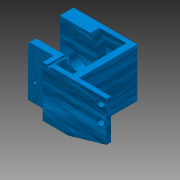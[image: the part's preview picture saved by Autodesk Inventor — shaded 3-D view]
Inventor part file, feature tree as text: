
AUTODESK INVENTOR PART (.ipt)
format: ipt  version: 2015 (Build 190159000, 159)  size: 166,400 bytes
history: native  units: in
note: dims shown in document units (in); Inventor stores cm internally (conversion verified against a paired STEP export)
features: sketch x10, other x3
ambient origin geometry x8: Origin, YZ Plane, XZ Plane, XY Plane, X Axis, Y Axis, Z Axis, Center Point
bodies: Solid1 (feature_tree)
feature tree (13):
  other  "Encoder Mount v2.ipt"
  other  "Solid1::Encoder Mount v2.ipt"
  other  "TaggingFeature1"
  sketch  "Sketch1"  dims[d0=0.3937in]
  sketch  "Sketch2"
  sketch  "Sketch3"
  sketch  "Sketch4"
  sketch  "Sketch5"
  sketch  "Sketch6"
  sketch  "Sketch7"
  sketch  "Sketch8"
  sketch  "Sketch9"
  sketch  "Sketch10"
